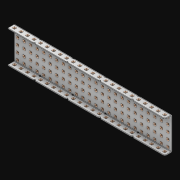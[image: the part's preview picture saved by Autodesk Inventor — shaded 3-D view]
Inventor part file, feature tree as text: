
AUTODESK INVENTOR PART (.ipt)
format: ipt  version: 2021 (Build 250183000, 183)  size: 3,547,136 bytes
history: native  units: in
note: dims shown in document units (in); Inventor stores cm internally (conversion verified against a paired STEP export)
features: extrude x169, other x168, sketch x4, thicken_offset x3, pattern_linear x3, imported_body x1
ambient origin geometry x8: Origin, YZ Plane, XZ Plane, XY Plane, X Axis, Y Axis, Z Axis, Center Point
bodies: Solid1 (feature_tree)
feature tree (348):
  thicken_offset  "Thicken1"
  thicken_offset  "Thicken2"
  thicken_offset  "Thicken3"
  pattern_linear  "Rectangular Pattern1"  Spacing1=0.001in  [1 undecoded]
  pattern_linear  "Rectangular Pattern2"  Spacing1=0.001in  [1 undecoded]
  pattern_linear  "Rectangular Pattern3"  Spacing1=0.182in  [1 undecoded]
  extrude  "Extrusion1"  Depth=0.063in TaperAngle=0.0deg
  sketch  "Sketch1"  dims[d0=0.001in]
  other  "Srf1"
  sketch  "Sketch2"  dims[d1=0.001in]
  other  "Srf2"
  sketch  "Sketch3"  dims[d2=0.001in]
  other  "Srf3"
  other  "Srf4"
  other  "Srf5"
  other  "Srf6"
  other  "Srf7"
  other  "Srf8"
  other  "Srf9"
  other  "Srf10"
  other  "Srf11"
  other  "Srf12"
  other  "Srf13"
  other  "Srf14"
  other  "Srf15"
  other  "Srf16"
  other  "Srf17"
  other  "Srf18"
  other  "Srf19"
  other  "Srf20"
  other  "Srf21"
  other  "Srf22"
  other  "Srf23"
  other  "Srf24"
  other  "Srf25"
  other  "Srf26"
  other  "Srf38"
  other  "Srf39"
  other  "Srf40"
  other  "Srf41"
  other  "Srf42"
  other  "Srf43"
  other  "Srf44"
  other  "Srf45"
  other  "Srf46"
  other  "Srf47"
  other  "Srf48"
  other  "Srf49"
  other  "Srf50"
  other  "Srf51"
  other  "Srf52"
  other  "Srf53"
  other  "Srf54"
  other  "Srf55"
  other  "Srf56"
  other  "Srf57"
  other  "Srf58"
  other  "Srf59"
  other  "Srf60"
  other  "Srf72"
  other  "Srf73"
  other  "Srf74"
  other  "Srf75"
  other  "Srf76"
  other  "Srf77"
  other  "Srf78"
  other  "Srf79"
  other  "Srf80"
  other  "Srf81"
  other  "Srf82"
  other  "Srf83"
  other  "Srf84"
  other  "Srf85"
  other  "Srf86"
  other  "Srf87"
  other  "Srf88"
  other  "Srf89"
  other  "Srf90"
  other  "Srf91"
  other  "Srf92"
  other  "Srf93"
  other  "Srf94"
  other  "Srf106"
  other  "Srf107"
  other  "Srf108"
  other  "Srf109"
  other  "Srf110"
  other  "Srf111"
  other  "Srf112"
  other  "Srf113"
  other  "Srf114"
  other  "Srf115"
  other  "Srf116"
  other  "Srf117"
  other  "Srf118"
  other  "Srf119"
  other  "Srf120"
  other  "Srf121"
  other  "Srf122"
  other  "Srf123"
  other  "Srf124"
  other  "Srf125"
  other  "Srf126"
  other  "Srf127"
  other  "Srf128"
  other  "Srf129"
  other  "Srf141"
  other  "Srf142"
  other  "Srf143"
  other  "Srf144"
  other  "Srf145"
  other  "Srf146"
  other  "Srf147"
  other  "Srf148"
  other  "Srf149"
  other  "Srf150"
  other  "Srf151"
  other  "Srf152"
  other  "Srf153"
  other  "Srf154"
  other  "Srf155"
  other  "Srf156"
  other  "Srf157"
  other  "Srf158"
  other  "Srf159"
  other  "Srf160"
  other  "Srf161"
  other  "Srf162"
  other  "Srf163"
  other  "Srf164"
  other  "Srf176"
  other  "Srf177"
  other  "Srf178"
  other  "Srf179"
  other  "Srf180"
  other  "Srf181"
  other  "Srf182"
  other  "Srf183"
  other  "Srf184"
  other  "Srf185"
  other  "Srf186"
  other  "Srf187"
  other  "Srf188"
  other  "Srf189"
  other  "Srf190"
  other  "Srf191"
  other  "Srf192"
  other  "Srf193"
  other  "Srf194"
  other  "Srf195"
  other  "Srf196"
  other  "Srf197"
  other  "Srf198"
  other  "Srf199"
  other  "Srf211"
  other  "Srf212"
  other  "Srf213"
  other  "Srf214"
  other  "Srf215"
  other  "Srf216"
  other  "Srf217"
  other  "Srf218"
  other  "Srf219"
  other  "Srf220"
  other  "Srf221"
  other  "Srf222"
  other  "Srf223"
  other  "Srf224"
  other  "Srf225"
  other  "Srf226"
  other  "Srf227"
  other  "Srf228"
  other  "Srf229"
  other  "Srf230"
  other  "Srf231"
  other  "Srf232"
  other  "Srf233"
  other  "Srf234"
  sketch  "Sketch4"  dims[d3=0.001in d4=0.001in d5=0.001in d6=0.182in d7=0.063in d8=0.0in d9=0.182in d10=0.063in d11=0.0in d12=0.182in d13=0.063in d14=0.0in d17=0.5in d18=9.4488in d20=0.5in d21=9.4488in d23=0.5in d24=1.9685in d26=0.5in d27=5.5in d28=0.0in]
  imported_body  "Imported1"
  extrude  "ExtrusionSrf1"  Depth=5.5in
  extrude  "ExtrusionSrf2"  Depth=0.063in TaperAngle=0.0deg
  extrude  "ExtrusionSrf3"  Depth=5.5in
  extrude  "ExtrusionSrf4"  Depth=0.063in TaperAngle=0.0deg
  extrude  "ExtrusionSrf5"  Depth=0.5in
  extrude  "ExtrusionSrf6"  Depth=5.5in
  extrude  "ExtrusionSrf7"  Depth=0.5in
  extrude  "ExtrusionSrf8"  Depth=5.5in
  extrude  "ExtrusionSrf9"  Depth=0.5in
  extrude  "ExtrusionSrf10"  Depth=0.5in
  extrude  "ExtrusionSrf11"  Depth=5.5in
  extrude  "ExtrusionSrf12"  TaperAngle=0.0deg  [1 undecoded]
  extrude  "ExtrusionSrf13"  [1 undecoded]
  extrude  "ExtrusionSrf14"  [1 undecoded]
  extrude  "ExtrusionSrf15"  [1 undecoded]
  extrude  "ExtrusionSrf16"  [1 undecoded]
  extrude  "ExtrusionSrf17"  [1 undecoded]
  extrude  "ExtrusionSrf18"  [1 undecoded]
  extrude  "ExtrusionSrf19"  [1 undecoded]
  extrude  "ExtrusionSrf20"  [1 undecoded]
  extrude  "ExtrusionSrf21"  [1 undecoded]
  extrude  "ExtrusionSrf22"  [1 undecoded]
  extrude  "ExtrusionSrf23"  [1 undecoded]
  extrude  "ExtrusionSrf24"  [1 undecoded]
  extrude  "ExtrusionSrf25"  [1 undecoded]
  extrude  "ExtrusionSrf26"  [1 undecoded]
  extrude  "ExtrusionSrf38"  [1 undecoded]
  extrude  "ExtrusionSrf39"  [1 undecoded]
  extrude  "ExtrusionSrf40"  [1 undecoded]
  extrude  "ExtrusionSrf41"  [1 undecoded]
  extrude  "ExtrusionSrf42"  [1 undecoded]
  extrude  "ExtrusionSrf43"  [1 undecoded]
  extrude  "ExtrusionSrf44"  [1 undecoded]
  extrude  "ExtrusionSrf45"  [1 undecoded]
  extrude  "ExtrusionSrf46"  [1 undecoded]
  extrude  "ExtrusionSrf47"  [1 undecoded]
  extrude  "ExtrusionSrf48"  [1 undecoded]
  extrude  "ExtrusionSrf49"  [1 undecoded]
  extrude  "ExtrusionSrf50"  [1 undecoded]
  extrude  "ExtrusionSrf51"  [1 undecoded]
  extrude  "ExtrusionSrf52"  [1 undecoded]
  extrude  "ExtrusionSrf53"  [1 undecoded]
  extrude  "ExtrusionSrf54"  [1 undecoded]
  extrude  "ExtrusionSrf55"  [1 undecoded]
  extrude  "ExtrusionSrf56"  [1 undecoded]
  extrude  "ExtrusionSrf57"  [1 undecoded]
  extrude  "ExtrusionSrf58"  [1 undecoded]
  extrude  "ExtrusionSrf59"  [1 undecoded]
  extrude  "ExtrusionSrf60"  [1 undecoded]
  extrude  "ExtrusionSrf72"  [1 undecoded]
  extrude  "ExtrusionSrf73"  [1 undecoded]
  extrude  "ExtrusionSrf74"  [1 undecoded]
  extrude  "ExtrusionSrf75"  [1 undecoded]
  extrude  "ExtrusionSrf76"  [1 undecoded]
  extrude  "ExtrusionSrf77"  [1 undecoded]
  extrude  "ExtrusionSrf78"  [1 undecoded]
  extrude  "ExtrusionSrf79"  [1 undecoded]
  extrude  "ExtrusionSrf80"  [1 undecoded]
  extrude  "ExtrusionSrf81"  [1 undecoded]
  extrude  "ExtrusionSrf82"  [1 undecoded]
  extrude  "ExtrusionSrf83"  [1 undecoded]
  extrude  "ExtrusionSrf84"  [1 undecoded]
  extrude  "ExtrusionSrf85"  [1 undecoded]
  extrude  "ExtrusionSrf86"  [1 undecoded]
  extrude  "ExtrusionSrf87"  [1 undecoded]
  extrude  "ExtrusionSrf88"  [1 undecoded]
  extrude  "ExtrusionSrf89"  [1 undecoded]
  extrude  "ExtrusionSrf90"  [1 undecoded]
  extrude  "ExtrusionSrf91"  [1 undecoded]
  extrude  "ExtrusionSrf92"  [1 undecoded]
  extrude  "ExtrusionSrf93"  [1 undecoded]
  extrude  "ExtrusionSrf94"  [1 undecoded]
  extrude  "ExtrusionSrf106"  [1 undecoded]
  extrude  "ExtrusionSrf107"  [1 undecoded]
  extrude  "ExtrusionSrf108"  [1 undecoded]
  extrude  "ExtrusionSrf109"  [1 undecoded]
  extrude  "ExtrusionSrf110"  [1 undecoded]
  extrude  "ExtrusionSrf111"  [1 undecoded]
  extrude  "ExtrusionSrf112"  [1 undecoded]
  extrude  "ExtrusionSrf113"  [1 undecoded]
  extrude  "ExtrusionSrf114"  [1 undecoded]
  extrude  "ExtrusionSrf115"  [1 undecoded]
  extrude  "ExtrusionSrf116"  [1 undecoded]
  extrude  "ExtrusionSrf117"  [1 undecoded]
  extrude  "ExtrusionSrf118"  [1 undecoded]
  extrude  "ExtrusionSrf119"  [1 undecoded]
  extrude  "ExtrusionSrf120"  [1 undecoded]
  extrude  "ExtrusionSrf121"  [1 undecoded]
  extrude  "ExtrusionSrf122"  [1 undecoded]
  extrude  "ExtrusionSrf123"  [1 undecoded]
  extrude  "ExtrusionSrf124"  [1 undecoded]
  extrude  "ExtrusionSrf125"  [1 undecoded]
  extrude  "ExtrusionSrf126"  [1 undecoded]
  extrude  "ExtrusionSrf127"  [1 undecoded]
  extrude  "ExtrusionSrf128"  [1 undecoded]
  extrude  "ExtrusionSrf129"  [1 undecoded]
  extrude  "ExtrusionSrf141"  [1 undecoded]
  extrude  "ExtrusionSrf142"  [1 undecoded]
  extrude  "ExtrusionSrf143"  [1 undecoded]
  extrude  "ExtrusionSrf144"  [1 undecoded]
  extrude  "ExtrusionSrf145"  [1 undecoded]
  extrude  "ExtrusionSrf146"  [1 undecoded]
  extrude  "ExtrusionSrf147"  [1 undecoded]
  extrude  "ExtrusionSrf148"  [1 undecoded]
  extrude  "ExtrusionSrf149"  [1 undecoded]
  extrude  "ExtrusionSrf150"  [1 undecoded]
  extrude  "ExtrusionSrf151"  [1 undecoded]
  extrude  "ExtrusionSrf152"  [1 undecoded]
  extrude  "ExtrusionSrf153"  [1 undecoded]
  extrude  "ExtrusionSrf154"  [1 undecoded]
  extrude  "ExtrusionSrf155"  [1 undecoded]
  extrude  "ExtrusionSrf156"  [1 undecoded]
  extrude  "ExtrusionSrf157"  [1 undecoded]
  extrude  "ExtrusionSrf158"  [1 undecoded]
  extrude  "ExtrusionSrf159"  [1 undecoded]
  extrude  "ExtrusionSrf160"  [1 undecoded]
  extrude  "ExtrusionSrf161"  [1 undecoded]
  extrude  "ExtrusionSrf162"  [1 undecoded]
  extrude  "ExtrusionSrf163"  [1 undecoded]
  extrude  "ExtrusionSrf164"  [1 undecoded]
  extrude  "ExtrusionSrf176"  [1 undecoded]
  extrude  "ExtrusionSrf177"  [1 undecoded]
  extrude  "ExtrusionSrf178"  [1 undecoded]
  extrude  "ExtrusionSrf179"  [1 undecoded]
  extrude  "ExtrusionSrf180"  [1 undecoded]
  extrude  "ExtrusionSrf181"  [1 undecoded]
  extrude  "ExtrusionSrf182"  [1 undecoded]
  extrude  "ExtrusionSrf183"  [1 undecoded]
  extrude  "ExtrusionSrf184"  [1 undecoded]
  extrude  "ExtrusionSrf185"  [1 undecoded]
  extrude  "ExtrusionSrf186"  [1 undecoded]
  extrude  "ExtrusionSrf187"  [1 undecoded]
  extrude  "ExtrusionSrf188"  [1 undecoded]
  extrude  "ExtrusionSrf189"  [1 undecoded]
  extrude  "ExtrusionSrf190"  [1 undecoded]
  extrude  "ExtrusionSrf191"  [1 undecoded]
  extrude  "ExtrusionSrf192"  [1 undecoded]
  extrude  "ExtrusionSrf193"  [1 undecoded]
  extrude  "ExtrusionSrf194"  [1 undecoded]
  extrude  "ExtrusionSrf195"  [1 undecoded]
  extrude  "ExtrusionSrf196"  [1 undecoded]
  extrude  "ExtrusionSrf197"  [1 undecoded]
  extrude  "ExtrusionSrf198"  [1 undecoded]
  extrude  "ExtrusionSrf199"  [1 undecoded]
  extrude  "ExtrusionSrf211"  [1 undecoded]
  extrude  "ExtrusionSrf212"  [1 undecoded]
  extrude  "ExtrusionSrf213"  [1 undecoded]
  extrude  "ExtrusionSrf214"  [1 undecoded]
  extrude  "ExtrusionSrf215"  [1 undecoded]
  extrude  "ExtrusionSrf216"  [1 undecoded]
  extrude  "ExtrusionSrf217"  [1 undecoded]
  extrude  "ExtrusionSrf218"  [1 undecoded]
  extrude  "ExtrusionSrf219"  [1 undecoded]
  extrude  "ExtrusionSrf220"  [1 undecoded]
  extrude  "ExtrusionSrf221"  [1 undecoded]
  extrude  "ExtrusionSrf222"  [1 undecoded]
  extrude  "ExtrusionSrf223"  [1 undecoded]
  extrude  "ExtrusionSrf224"  [1 undecoded]
  extrude  "ExtrusionSrf225"  [1 undecoded]
  extrude  "ExtrusionSrf226"  [1 undecoded]
  extrude  "ExtrusionSrf227"  [1 undecoded]
  extrude  "ExtrusionSrf228"  [1 undecoded]
  extrude  "ExtrusionSrf229"  [1 undecoded]
  extrude  "ExtrusionSrf230"  [1 undecoded]
  extrude  "ExtrusionSrf231"  [1 undecoded]
  extrude  "ExtrusionSrf232"  [1 undecoded]
  extrude  "ExtrusionSrf233"  [1 undecoded]
  extrude  "ExtrusionSrf234"  [1 undecoded]
note: 160 required parameter values undecoded (feature->parameter linkage not recoverable at this tier; creation-order binding heuristic only, values carry confidence <= 0.55)
